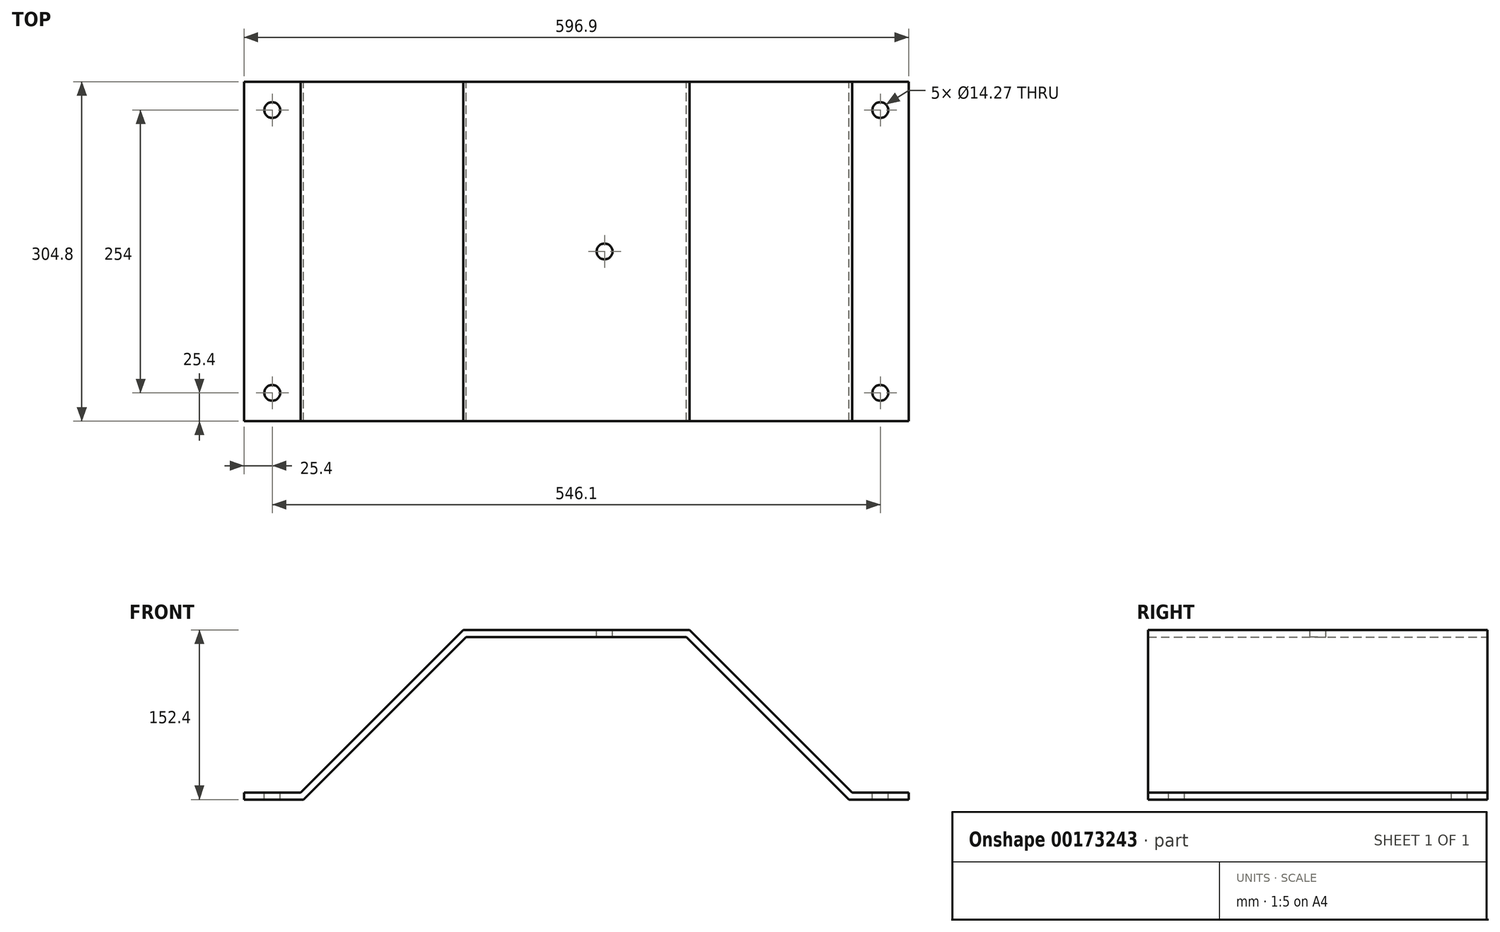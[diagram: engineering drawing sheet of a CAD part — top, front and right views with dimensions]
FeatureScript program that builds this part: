
annotation { "Feature Type Name" : "Feature", "Feature Type Description" : "" }
export const myFeature = defineFeature(function(context is Context, id is Id, definition is map)
    precondition{}
    {
        {
            var Q0;
            Q0=qCreatedBy(makeId("Front.planeOp"),FACE);
            var sketch = newSketch(context, id + "F0", { "sketchPlane" : qUnion([Q0])});
            skLineSegment(sketch, "E0", {"start": v(-101.6, 0) * mm, "end": v(101.6, 0) * mm});
            skLineSegment(sketch, "E1", {"start": v(101.6, 0) * mm, "end": v(247.65, -146.05) * mm});
            skLineSegment(sketch, "E2", {"start": v(247.65, -146.05) * mm, "end": v(298.45, -146.05) * mm});
            skLineSegment(sketch, "E3", {"start": v(298.45, -146.05) * mm, "end": v(298.45, -152.4) * mm});
            skLineSegment(sketch, "E4", {"start": v(298.45, -152.4) * mm, "end": v(245.02, -152.4) * mm});
            skLineSegment(sketch, "E5", {"start": v(245.02, -152.4) * mm, "end": v(98.97, -6.35) * mm});
            skLineSegment(sketch, "E6", {"start": v(98.97, -6.35) * mm, "end": v(-98.97, -6.35) * mm});
            skLineSegment(sketch, "E7", {"start": v(-98.97, -6.35) * mm, "end": v(-245.02, -152.4) * mm});
            skLineSegment(sketch, "E8", {"start": v(-245.02, -152.4) * mm, "end": v(-298.45, -152.4) * mm});
            skLineSegment(sketch, "E9", {"start": v(-298.45, -152.4) * mm, "end": v(-298.45, -146.05) * mm});
            skLineSegment(sketch, "E10", {"start": v(-298.45, -146.05) * mm, "end": v(-247.65, -146.05) * mm});
            skLineSegment(sketch, "E11", {"start": v(-247.65, -146.05) * mm, "end": v(-101.6, 0) * mm});
            skSolve(sketch);
        }
        {
            var Q0;
            Q0 = qSketchRegion(id + "F0", true);
            extrude(context, id + "F1", {"entities" : qUnion([Q0]), "endBound" : BoundingType.SYMMETRIC, "depth" : 304.8 * mm});
        }
        {
            var Q0;
            Q0=makeQuery(id+"F1.opExtrude","SWEPT_FACE",FACE,{"disambiguationData":[OSD([sQuery(id+"F0.wireOp",EDGE,"E10")])]});
            var sketch = newSketch(context, id + "F2", { "sketchPlane" : qUnion([Q0])});
            skCircle(sketch, "E12", {"center": v(-273.05, -127) * mm, "radius": 7.14 * mm});
            skLineSegment(sketch, "E13", {"start": v(0, 153.5) * mm, "end": v(0, -152.33) * mm});
            skLineSegment(sketch, "E14", {"start": v(-298.45, 0) * mm, "end": v(297.7, 0) * mm});
            skPoint(sketch, "E14.endSnap0", {"position": v(-298.45, 0) * mm});
            skCircle(sketch, "E15.MirrorC", {"center": v(-273.05, 127) * mm, "radius": 7.14 * mm});
            skCircle(sketch, "E16.MirrorC", {"center": v(273.05, -127) * mm, "radius": 7.14 * mm});
            skCircle(sketch, "E17.MirrorC", {"center": v(273.05, 127) * mm, "radius": 7.14 * mm});
            skSolve(sketch);
        }
        {
            var Q0;
            Q0 = qSketchRegion(id + "F2", true);
            extrude(context, id + "F3", {"entities" : qUnion([Q0]), "operationType" : NewBodyOperationType.REMOVE, "endBound" : BoundingType.THROUGH_ALL, "oppositeDirection" : true, "depth" : 25.4 * mm});
        }
        {
            var Q0;
            Q0=makeQuery(id+"F1.opExtrude","SWEPT_FACE",FACE,{"disambiguationData":[OSD([sQuery(id+"F0.wireOp",EDGE,"E0")])]});
            var sketch = newSketch(context, id + "F4", { "sketchPlane" : qUnion([Q0])});
            skCircle(sketch, "E18", {"center": v(25.4, 0) * mm, "radius": 7.14 * mm});
            skSolve(sketch);
        }
        {
            var Q0;
            Q0 = qSketchRegion(id + "F4", true);
            extrude(context, id + "F5", {"entities" : qUnion([Q0]), "operationType" : NewBodyOperationType.REMOVE, "endBound" : BoundingType.THROUGH_ALL, "oppositeDirection" : true, "depth" : 25.4 * mm});
        }
    });
